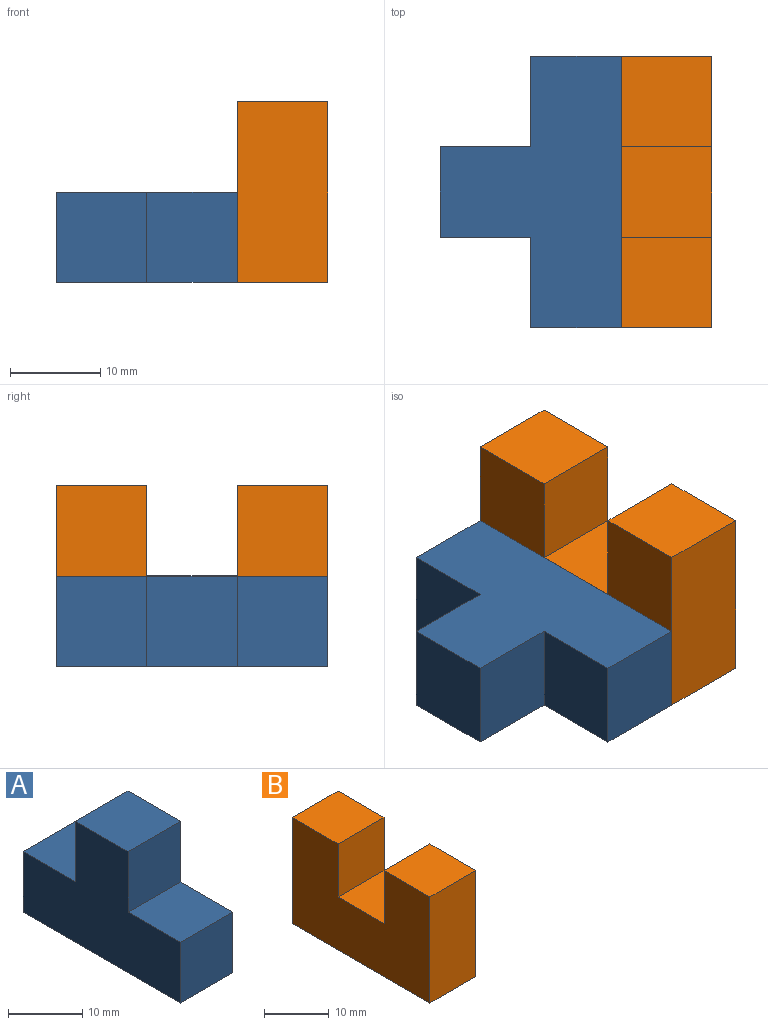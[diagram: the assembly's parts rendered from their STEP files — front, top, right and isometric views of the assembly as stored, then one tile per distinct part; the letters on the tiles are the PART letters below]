
ASSEMBLY  parts=2 mates=1
PART A: 10 faces, bbox 10x30x20 mm
  f0: plane 30x20mm, normal (1,0,0), area 400mm2, adj f1,f3,f4,f5,f6,f7,f8,f9
  f1: plane 10x10mm, normal (0,1,0), area 100mm2, adj f0,f2,f7,f8
  f2: plane 30x20mm, normal (-1,0,0), area 400mm2, adj f1,f3,f4,f5,f6,f7,f8,f9
  f3: plane 10x10mm, normal (0,0,1), area 100mm2, adj f0,f2,f4,f5
  f4: plane 10x10mm, normal (0,1,0), area 100mm2, adj f0,f2,f3,f7
  f5: plane 10x10mm, normal (0,-1,0), area 100mm2, adj f0,f2,f3,f6
  f6: plane 10x10mm, normal (0,0,1), area 100mm2, adj f0,f2,f5,f9
  f7: plane 10x10mm, normal (0,0,1), area 100mm2, adj f0,f1,f2,f4
  f8: plane 30x10mm, normal (0,0,-1), area 300mm2, adj f0,f1,f2,f9
  f9: plane 10x10mm, normal (0,-1,0), area 100mm2, adj f0,f2,f6,f8
PART B: 10 faces, bbox 10x30x20 mm
  f0: plane 10x10mm, normal (0,1,0), area 100mm2, adj f1,f2,f4,f6
  f1: plane 10x10mm, normal (0,0,1), area 100mm2, adj f0,f2,f4,f5
  f2: plane 30x20mm, normal (-1,0,0), area 500mm2, adj f0,f1,f3,f5,f6,f7,f8,f9
  f3: plane 30x10mm, normal (0,0,-1), area 300mm2, adj f2,f4,f5,f8
  f4: plane 30x20mm, normal (1,0,0), area 500mm2, adj f0,f1,f3,f5,f6,f7,f8,f9
  f5: plane 20x10mm, normal (0,-1,0), area 200mm2, adj f1,f2,f3,f4
  f6: plane 10x10mm, normal (0,0,1), area 100mm2, adj f0,f2,f4,f7
  f7: plane 10x10mm, normal (0,-1,0), area 100mm2, adj f2,f4,f6,f9
  f8: plane 20x10mm, normal (0,1,0), area 200mm2, adj f2,f3,f4,f9
  f9: plane 10x10mm, normal (0,0,1), area 100mm2, adj f2,f4,f7,f8
PLACE A rot(axis=(0,-1,0),90deg) t=(14.49,8.84,2.52)mm
PLACE B t=(62.45,8.84,-16.1)mm
MATE fastened A.f8 <-> B.f2  axis (1,0,0) through (21.39,-1.16,-2.1)mm
